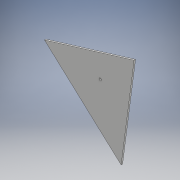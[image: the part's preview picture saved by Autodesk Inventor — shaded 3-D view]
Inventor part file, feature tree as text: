
AUTODESK INVENTOR PART (.ipt)
format: ipt  version: 2018.2 (Build 222227000, 227)  size: 92,160 bytes
history: native  units: mm
features: other x1, extrude x1, sketch x1
ambient origin geometry x8: Origin, YZ Plane, XZ Plane, XY Plane, X Axis, Y Axis, Z Axis, Center Point
bodies: Body1 (feature_tree)
feature tree (3):
  other  "ソリッド1"
  extrude  "押し出し1"  Depth=5.0mm
  sketch  "スケッチ1"
